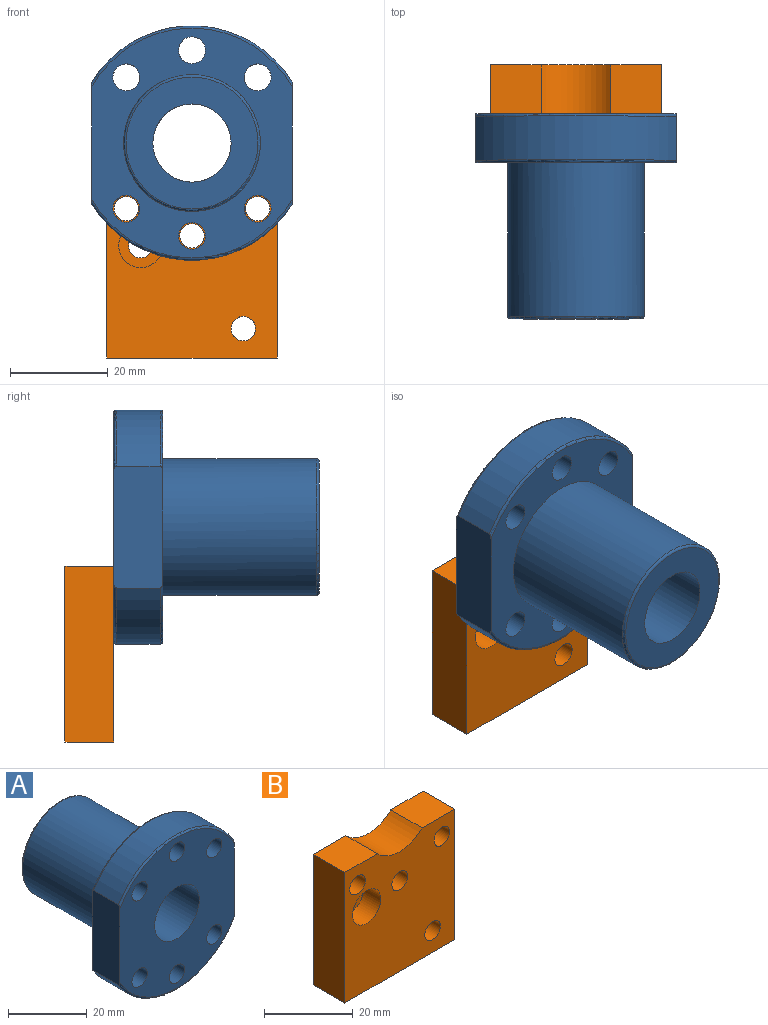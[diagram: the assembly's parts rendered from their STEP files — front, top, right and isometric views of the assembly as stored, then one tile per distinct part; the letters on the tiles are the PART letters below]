
ASSEMBLY  parts=2 mates=1
PART A: 20 faces, bbox 45.3x42x52 mm
  f0: plane 47x41mm, normal (0,-1,0), area 1298.2mm2, adj f2,f4,f6,f7,f8,f9,f10,f11
  f1: plane 47x41mm, normal (0,1,0), area 883.5mm2, adj f2,f4,f6,f7,f8,f9,f10,f11
  f2: plane 24.96x10mm, normal (1,0,0), area 249.2mm2, adj f0,f1,f3,f5,f16,f17,f18,f19
  f3: cylinder r=24mm len=41mm, axis (0,1,0), area 442.3mm2, adj f2,f4,f16,f18
  f4: plane 24.96x10mm, normal (-1,0,0), area 249.2mm2, adj f0,f1,f3,f5,f16,f17,f18,f19
  f5: cylinder r=24mm len=41mm, axis (0,1,0), area 442.3mm2, adj f2,f4,f17,f19
  f6: cylinder r=2.75mm len=10mm, axis (0,-1,0), area 172.8mm2, adj f0,f1
  f7: cylinder r=2.75mm len=10mm, axis (0,-1,0), area 172.8mm2, adj f0,f1
  f8: cylinder r=2.75mm len=10mm, axis (0,-1,0), area 172.8mm2, adj f0,f1
  f9: cylinder r=2.75mm len=10mm, axis (0,-1,0), area 172.8mm2, adj f0,f1
  f10: cylinder r=2.75mm len=10mm, axis (0,-1,0), area 172.8mm2, adj f0,f1
  f11: cylinder r=2.75mm len=10mm, axis (0,-1,0), area 172.8mm2, adj f0,f1
  f12: cylinder r=14mm len=31.5mm, axis (0,-1,0), area 2770.9mm2, adj f1,f15
  f13: plane 27x27mm, normal (0,1,0), area 371.5mm2, adj f14,f15
  f14: cylinder r=8mm len=42mm, axis (0,-1,0), area 2111.2mm2, adj f0,f13
  f15: torus R=13.5mm, axis (0,1,0), area 68.2mm2, adj f12,f13
  f16: torus R=23.5mm, axis (0,-1,0), area 38.8mm2, adj f1,f2,f3,f4
  f17: torus R=23.5mm, axis (0,-1,0), area 38.8mm2, adj f1,f2,f4,f5
  f18: torus R=23.5mm, axis (0,-1,0), area 38.8mm2, adj f0,f2,f3,f4
  f19: torus R=23.5mm, axis (0,-1,0), area 38.8mm2, adj f0,f2,f4,f5
PART B: 15 faces, bbox 35x10x36 mm
  f0: cylinder r=2.5mm len=5mm, axis (0,-1,0), area 70.7mm2, adj f4,f13
  f1: plane 36x10mm, normal (-1,0,0), area 360mm2, adj f3,f4,f5,f12
  f2: plane 36x10mm, normal (1,0,0), area 360mm2, adj f3,f4,f5,f11
  f3: plane 36x35mm, normal (0,-1,0), area 1088.3mm2, adj f1,f2,f5,f6,f7,f8,f9,f10
  f4: plane 36x35mm, normal (0,1,0), area 1132.3mm2, adj f0,f1,f2,f5,f6,f7,f8,f9
  f5: plane 35x10mm, normal (0,0,-1), area 350mm2, adj f1,f2,f3,f4
  f6: cylinder r=2.5mm len=10mm, axis (0,-1,0), area 157.1mm2, adj f3,f4
  f7: cylinder r=2.5mm len=10mm, axis (0,-1,0), area 157.1mm2, adj f3,f4
  f8: cylinder r=2.5mm len=10mm, axis (0,-1,0), area 157.1mm2, adj f3,f4
  f9: cylinder r=2.5mm len=10mm, axis (0,-1,0), area 157.1mm2, adj f3,f4
  f10: cylinder r=10mm len=14.28mm, axis (0,-1,0), area 159.1mm2, adj f3,f4,f11,f12
  f11: plane 10.36x10mm, normal (0,0,1), area 103.6mm2, adj f2,f3,f4,f10
  f12: plane 10.36x10mm, normal (0,0,1), area 103.6mm2, adj f1,f3,f4,f10
  f13: plane 9x9mm, normal (0,-1,0), area 44mm2, adj f0,f14
  f14: cylinder r=4.5mm len=9mm, axis (0,-1,0), area 155.5mm2, adj f3,f13
PLACE A rot(axis=(0,0,1),180deg) t=(17.5,-10,43)mm
PLACE B t=(0,0,-1)mm
MATE fastened A.f10 <-> B.f9  axis (0,1,0) through (17.5,0,24)mm
